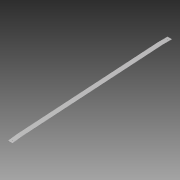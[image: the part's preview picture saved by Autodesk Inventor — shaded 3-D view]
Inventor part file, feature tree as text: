
AUTODESK INVENTOR PART (.ipt)
format: ipt  version: 2014 (Build 180170000, 170)  size: 169,472 bytes
history: native  units: in
note: dims shown in document units (in); Inventor stores cm internally (conversion verified against a paired STEP export)
features: sketch x6, hole x3, sheet_metal_op x2, extrude x1, other x1
ambient origin geometry x8: Origin, YZ Plane, XZ Plane, XY Plane, X Axis, Y Axis, Z Axis, Center Point
bodies: Solid1 (feature_tree)
feature tree (13):
  extrude  "Extrusion1"  Depth=0.0394in
  hole  "Hole1"  [1 undecoded]
  hole  "Hole2"  [1 undecoded]
  sheet_metal_op  "Fold1"
  sheet_metal_op  "Fold3"
  hole  "Hole3"  [1 undecoded]
  sketch  "Sketch1"  dims[d0=1.5in d1=0.0394in]
  sketch  "Sketch2"  dims[d2=54.0157in d3=0.0in d4=0.7874in]
  sketch  "Sketch3"  dims[d5=0.1969in d6=0.75in d7=0.375in d8=0.25in d9=0.5635in d10=1.0in d11=0.8108in d12=0.7874in]
  sketch  "Sketch4"  dims[d13=0.1969in d14=0.75in d15=0.375in d16=0.25in d17=0.5635in d18=1.0in d19=0.8108in d20=2.3622in]
  sketch  "Sketch6"  dims[d21=0.0in]
  sketch  "Sketch7"  dims[d22=0.0394in d23=0.0197in d24=0.0787in d25=0.0394in d26=0.0254in d27=0.0394in d35=2.3622in d36=0.0in d37=0.0394in d38=0.0197in d39=0.0787in d40=0.0394in d41=0.0254in d42=0.0394in d43=5.9055in d44=0.0394in d45=0.2362in d46=0.1575in d47=0.0787in d48=90.0deg d49=0.0394in d50=0.8108in]
  other  "Definition1"
note: 3 required parameter values undecoded (feature->parameter linkage not recoverable at this tier; creation-order binding heuristic only, values carry confidence <= 0.55)
